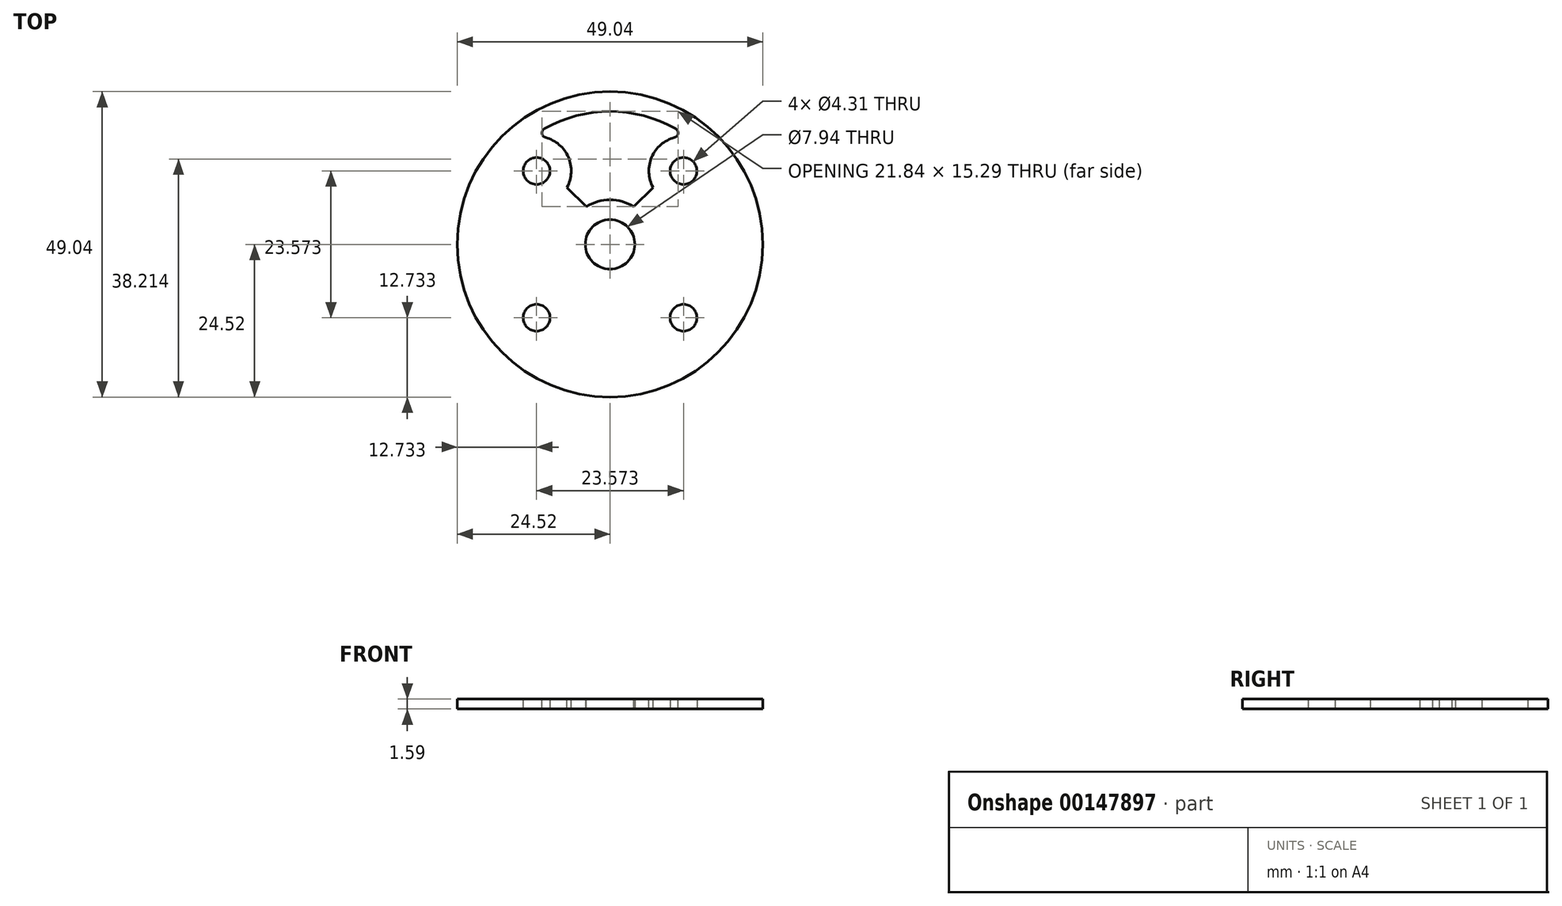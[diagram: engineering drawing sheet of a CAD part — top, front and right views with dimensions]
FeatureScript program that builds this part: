
annotation { "Feature Type Name" : "Feature", "Feature Type Description" : "" }
export const myFeature = defineFeature(function(context is Context, id is Id, definition is map)
    precondition{}
    {
        {
            var Q0;
            Q0=qCreatedBy(makeId("Top.planeOp"),FACE);
            var sketch = newSketch(context, id + "F0", { "sketchPlane" : qUnion([Q0])});
            skCircle(sketch, "E0", {"center": v(0, 0) * mm, "radius": 24.52 * mm});
            skCircle(sketch, "E1", {"center": v(0, 0) * mm, "radius": 3.97 * mm});
            skLineSegment(sketch, "E2.bottom", {"start": v(-11.79, 11.79) * mm, "end": v(11.79, 11.79) * mm, "construction": true});
            skLineSegment(sketch, "E2.top", {"start": v(-11.79, -11.79) * mm, "end": v(11.79, -11.79) * mm, "construction": true});
            skLineSegment(sketch, "E2.left", {"start": v(-11.79, 11.79) * mm, "end": v(-11.79, -11.79) * mm, "construction": true});
            skLineSegment(sketch, "E2.right", {"start": v(11.79, 11.79) * mm, "end": v(11.79, -11.79) * mm, "construction": true});
            skCircle(sketch, "E3", {"center": v(-11.79, 11.79) * mm, "radius": 7.85 * mm, "construction": true});
            skCircle(sketch, "E4", {"center": v(11.79, 11.79) * mm, "radius": 2.15 * mm});
            skCircle(sketch, "E5", {"center": v(-11.79, 11.79) * mm, "radius": 2.15 * mm});
            skCircle(sketch, "E6", {"center": v(-11.79, -11.79) * mm, "radius": 2.15 * mm});
            skCircle(sketch, "E7", {"center": v(11.79, -11.79) * mm, "radius": 2.15 * mm});
            skSolve(sketch);
        }
        {
            var Q0;
            Q0=qSketchRegion(id+"F0",true);
            extrude(context, id + "F1", {"entities" : qUnion([Q0]), "depth" : 1.59 * mm});
        }
        {
            var Q0;
            Q0=makeQuery(id+"F1.opExtrude","CAP_FACE",FACE,{"disambiguationData":[OSD([sQuery(id+"F0.wireOp",EDGE,"E0"),sQuery(id+"F0.wireOp",EDGE,"E1"),sQuery(id+"F0.wireOp",EDGE,"E4"),sQuery(id+"F0.wireOp",EDGE,"E5"),sQuery(id+"F0.wireOp",EDGE,"E6"),sQuery(id+"F0.wireOp",EDGE,"E7")])],"isStart":false});
            var sketch = newSketch(context, id + "F2", { "sketchPlane" : qUnion([Q0])});
            skArc(sketch, "E8", {"start": v(-6.9, 9.14) * mm, "mid": v(-7.2, 14.93) * mm, "end": v(-12.5, 17.3) * mm});
            skArc(sketch, "E9", {"start": v(12.5, 17.3) * mm, "mid": v(7.2, 14.93) * mm, "end": v(6.9, 9.14) * mm});
            skArc(sketch, "E10", {"start": v(12.5, 17.3) * mm, "mid": v(0, 21.34) * mm, "end": v(-12.5, 17.3) * mm});
            skArc(sketch, "E11", {"start": v(3.8, 6.05) * mm, "mid": v(0, 7.14) * mm, "end": v(-3.8, 6.05) * mm});
            skLineSegment(sketch, "E12.bottom", {"start": v(-9.14, 6.9) * mm, "end": v(-6.9, 9.14) * mm, "construction": true});
            skLineSegment(sketch, "E12.top", {"start": v(-6.05, 3.8) * mm, "end": v(-3.8, 6.05) * mm, "construction": true});
            skLineSegment(sketch, "E12.left", {"start": v(-9.14, 6.9) * mm, "end": v(-6.05, 3.8) * mm, "construction": true});
            skLineSegment(sketch, "E12.right", {"start": v(-6.9, 9.14) * mm, "end": v(-3.8, 6.05) * mm});
            skLineSegment(sketch, "E13.bottom", {"start": v(9.14, 6.9) * mm, "end": v(6.9, 9.14) * mm, "construction": true});
            skLineSegment(sketch, "E13.top", {"start": v(6.05, 3.8) * mm, "end": v(3.8, 6.05) * mm, "construction": true});
            skLineSegment(sketch, "E13.left", {"start": v(9.14, 6.9) * mm, "end": v(6.05, 3.8) * mm, "construction": true});
            skLineSegment(sketch, "E13.right", {"start": v(6.9, 9.14) * mm, "end": v(3.8, 6.05) * mm});
            skLineSegment(sketch, "E14", {"start": v(-8.02, 8.02) * mm, "end": v(-11.79, 11.79) * mm, "construction": true});
            skLineSegment(sketch, "E15", {"start": v(-4.93, 4.93) * mm, "end": v(0, 0) * mm, "construction": true});
            skLineSegment(sketch, "E16", {"start": v(0, 0) * mm, "end": v(4.93, 4.93) * mm, "construction": true});
            skLineSegment(sketch, "E17", {"start": v(8.02, 8.02) * mm, "end": v(11.79, 11.79) * mm, "construction": true});
            skSolve(sketch);
        }
        {
            var Q0;
            Q0=makeQuery(id+"F2.imprint","IMPRINT",FACE,{"disambiguationData":[TD([[makeQuery(id+"F2.imprint","IMPRINT",EDGE,{"derivedFrom":sQuery(id+"F2.wireOp",EDGE,"E8")}),-1.0]])]});
            var Q1;
            Q1=makeQuery(id+"F1.opExtrude","CAP_FACE",FACE,{"disambiguationData":[OSD([sQuery(id+"F0.wireOp",EDGE,"E0"),sQuery(id+"F0.wireOp",EDGE,"E1"),sQuery(id+"F0.wireOp",EDGE,"E4"),sQuery(id+"F0.wireOp",EDGE,"E5"),sQuery(id+"F0.wireOp",EDGE,"E6"),sQuery(id+"F0.wireOp",EDGE,"E7")])],"isStart":true});
            extrude(context, id + "F3", {"entities" : qUnion([Q0]), "operationType" : NewBodyOperationType.REMOVE, "endBound" : BoundingType.UP_TO_SURFACE, "oppositeDirection" : true, "endBoundEntityFace" : qUnion([Q1]), "depth" : 25.4 * mm});
        }
        {
            var Q0;
            Q0=makeQuery(id+"F6MqURjXbY15YYN_1.1.F3.boolean.opBoolean","COPY",EDGE,{"derivedFrom":makeQuery(id+"F6MqURjXbY15YYN_1.1.F3.opExtrude","SWEPT_EDGE",EDGE,{"disambiguationData":[OSD([sQuery(id+"F2.wireOp",EDGE,"E8"),sQuery(id+"F2.wireOp",EDGE,"E10")])]})});
            var Q1;
            Q1=makeQuery(id+"F6MqURjXbY15YYN_1.1.F3.boolean.opBoolean","COPY",EDGE,{"derivedFrom":makeQuery(id+"F6MqURjXbY15YYN_1.1.F3.opExtrude","SWEPT_EDGE",EDGE,{"disambiguationData":[OSD([sQuery(id+"F2.wireOp",EDGE,"E9"),sQuery(id+"F2.wireOp",EDGE,"E10")])]})});
            var Q2;
            Q2=makeQuery(id+"F6MqURjXbY15YYN_1.2.F3.boolean.opBoolean","COPY",EDGE,{"derivedFrom":makeQuery(id+"F6MqURjXbY15YYN_1.2.F3.opExtrude","SWEPT_EDGE",EDGE,{"disambiguationData":[OSD([sQuery(id+"F2.wireOp",EDGE,"E8"),sQuery(id+"F2.wireOp",EDGE,"E10")])]})});
            var Q3;
            Q3=makeQuery(id+"F6MqURjXbY15YYN_1.2.F3.boolean.opBoolean","COPY",EDGE,{"derivedFrom":makeQuery(id+"F6MqURjXbY15YYN_1.2.F3.opExtrude","SWEPT_EDGE",EDGE,{"disambiguationData":[OSD([sQuery(id+"F2.wireOp",EDGE,"E9"),sQuery(id+"F2.wireOp",EDGE,"E10")])]})});
            var Q4;
            Q4=makeQuery(id+"F6MqURjXbY15YYN_1.3.F3.boolean.opBoolean","COPY",EDGE,{"derivedFrom":makeQuery(id+"F6MqURjXbY15YYN_1.3.F3.opExtrude","SWEPT_EDGE",EDGE,{"disambiguationData":[OSD([sQuery(id+"F2.wireOp",EDGE,"E8"),sQuery(id+"F2.wireOp",EDGE,"E10")])]})});
            var Q5;
            Q5=makeQuery(id+"F6MqURjXbY15YYN_1.3.F3.boolean.opBoolean","COPY",EDGE,{"derivedFrom":makeQuery(id+"F6MqURjXbY15YYN_1.3.F3.opExtrude","SWEPT_EDGE",EDGE,{"disambiguationData":[OSD([sQuery(id+"F2.wireOp",EDGE,"E9"),sQuery(id+"F2.wireOp",EDGE,"E10")])]})});
            var Q6;
            Q6=makeQuery(id+"F3.boolean.opBoolean","COPY",EDGE,{"derivedFrom":makeQuery(id+"F3.opExtrude","SWEPT_EDGE",EDGE,{"disambiguationData":[OSD([sQuery(id+"F2.wireOp",EDGE,"E8"),sQuery(id+"F2.wireOp",EDGE,"E10")])]})});
            var Q7;
            Q7=makeQuery(id+"F3.boolean.opBoolean","COPY",EDGE,{"derivedFrom":makeQuery(id+"F3.opExtrude","SWEPT_EDGE",EDGE,{"disambiguationData":[OSD([sQuery(id+"F2.wireOp",EDGE,"E9"),sQuery(id+"F2.wireOp",EDGE,"E10")])]})});
            fillet(context, id + "F4", {"entities" : qUnion([Q0, Q1, Q2, Q3, Q4, Q5, Q6, Q7]), "radius" : 0.76 * mm, "tangentPropagation" : true, "allowEdgeOverflow" : false});
        }
    });
